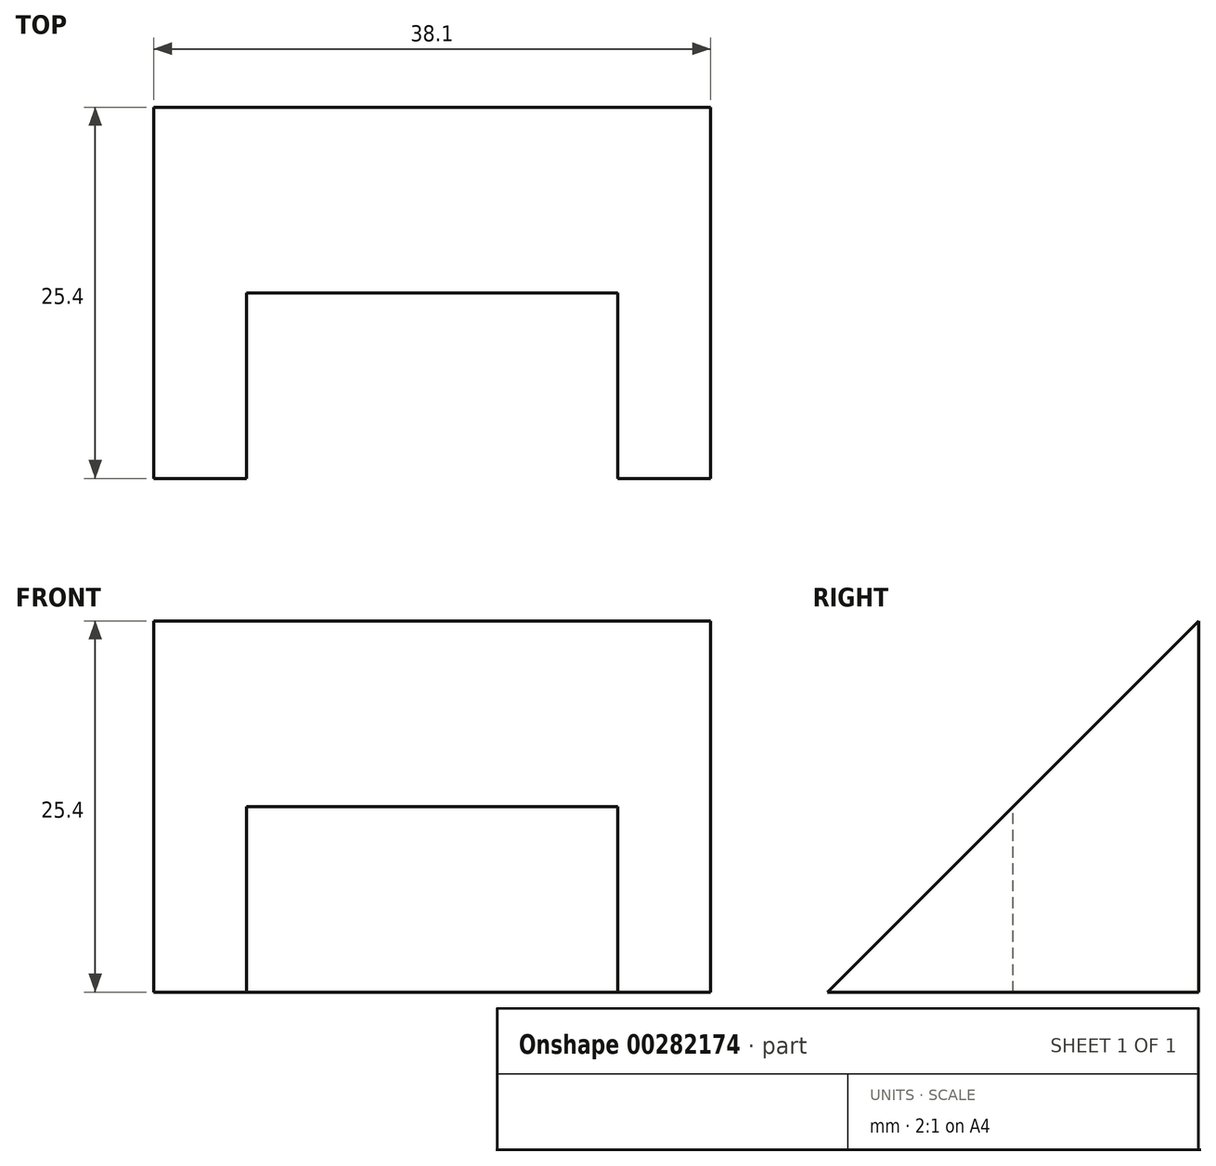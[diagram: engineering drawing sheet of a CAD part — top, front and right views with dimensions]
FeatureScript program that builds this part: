
annotation { "Feature Type Name" : "Feature", "Feature Type Description" : "" }
export const myFeature = defineFeature(function(context is Context, id is Id, definition is map)
    precondition{}
    {
        {
            var Q0;
            Q0=qCreatedBy(makeId("Right.planeOp"),FACE);
            var sketch = newSketch(context, id + "F0", { "sketchPlane" : qUnion([Q0])});
            skLineSegment(sketch, "E0", {"start": v(12.7, 25.4) * mm, "end": v(12.7, 0) * mm});
            skLineSegment(sketch, "E1", {"start": v(12.7, 0) * mm, "end": v(-12.7, 0) * mm});
            skLineSegment(sketch, "E2", {"start": v(-12.7, 0) * mm, "end": v(12.7, 25.4) * mm});
            skSolve(sketch);
        }
        {
            var Q0;
            Q0=makeQuery(id+"F0.imprint","IMPRINT",FACE,{"disambiguationData":[TD([[makeQuery(id+"F0.imprint","IMPRINT",EDGE,{"derivedFrom":sQuery(id+"F0.wireOp",EDGE,"E0")}),-1.0]])]});
            extrude(context, id + "F1", {"entities" : qUnion([Q0]), "oppositeDirection" : true, "depth" : 38.1 * mm});
        }
        {
            var Q0;
            Q0=makeQuery(id+"F1.opExtrude","CAP_FACE",FACE,{"disambiguationData":[OSD([sQuery(id+"F0.wireOp",EDGE,"E0"),sQuery(id+"F0.wireOp",EDGE,"E1"),sQuery(id+"F0.wireOp",EDGE,"E2")])],"isStart":true});
            var sketch = newSketch(context, id + "F2", { "sketchPlane" : qUnion([Q0])});
            skLineSegment(sketch, "E3", {"start": v(0, 12.7) * mm, "end": v(-12.7, 0) * mm});
            skLineSegment(sketch, "E4", {"start": v(-12.7, 0) * mm, "end": v(0, 0) * mm});
            skLineSegment(sketch, "E5", {"start": v(0, 0) * mm, "end": v(0, 12.7) * mm});
            skSolve(sketch);
        }
        {
            var Q0;
            Q0=makeQuery(id+"F2.imprint","IMPRINT",FACE,{"disambiguationData":[TD([[makeQuery(id+"F2.imprint","IMPRINT",EDGE,{"derivedFrom":sQuery(id+"F2.wireOp",EDGE,"E3")}),-1.0]])]});
            extrude(context, id + "F3", {"entities" : qUnion([Q0]), "operationType" : NewBodyOperationType.REMOVE, "oppositeDirection" : true, "depth" : 31.75 * mm, "hasSecondDirection" : true, "secondDirectionOppositeDirection" : true, "secondDirectionDepth" : 6.35 * mm});
        }
    });
